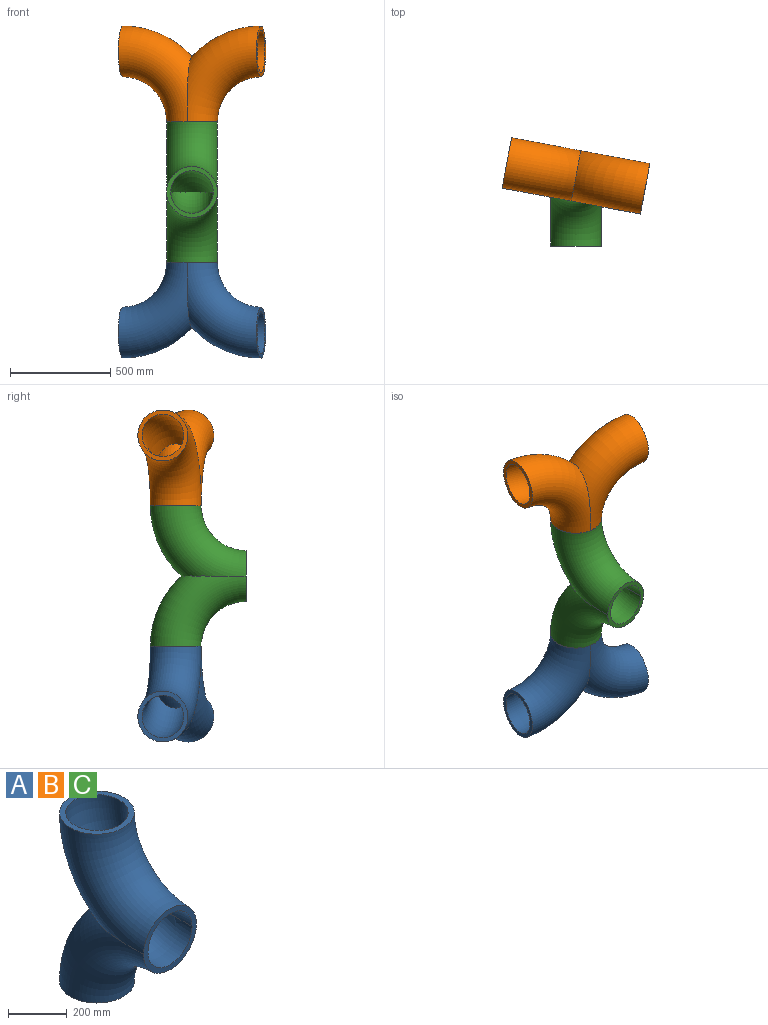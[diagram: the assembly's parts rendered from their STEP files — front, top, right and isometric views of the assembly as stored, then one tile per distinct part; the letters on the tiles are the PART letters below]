
ASSEMBLY  parts=3 mates=5
PART A: 11 faces, bbox 254x517.5x702.2 mm
  f0: torus R=351.08mm, axis (1,0,0), area 77600.1mm2, adj f3,f10
  f1: torus R=351.08mm, axis (1,0,0), area 240336.9mm2, adj f4,f9
  f2: torus R=351.08mm, axis (1,0,0), area 336108.5mm2, adj f3,f4,f7
  f3: plane 254x254mm, normal (0,-1,0), area 15428.1mm2, adj f0,f2,f7,f10
  f4: plane 254x254mm, normal (0,0,-1), area 15428.1mm2, adj f1,f2
  f5: torus R=351.08mm, axis (1,0,0), area 240340.8mm2, adj f6,f8
  f6: plane 254x254mm, normal (0,0,1), area 15428.1mm2, adj f5,f7
  f7: torus R=351.08mm, axis (1,0,0), area 336121.8mm2, adj f2,f3,f6
  f8: torus R=351.08mm, axis (1,0,0), area 48416.9mm2, adj f5
  f9: torus R=351.08mm, axis (1,0,0), area 48414.9mm2, adj f1
  f10: torus R=351.08mm, axis (1,0,0), area 77609.6mm2, adj f0,f3
PART B: same geometry as A
PART C: same geometry as A
PLACE A rot(axis=(-0.51,0.61,-0.61),126.3deg) t=(-404.48,689.43,29.83)mm
PLACE B rot(axis=(0.51,-0.61,-0.61),126.3deg) t=(-404.48,689.43,732)mm
PLACE C t=(-404.48,338.34,380.91)mm fixed
MATE cylindrical C.f6 <-> B.f3  axis (0,0,1) through (-404.48,689.43,732)mm
MATE planar B.f3 <-> C.f6  axis (0,0,-1) through (-404.48,689.43,732)mm
MATE cylindrical A.f3 <-> C.f4  axis (0,0,1) through (-404.48,689.43,29.83)mm
MATE planar C.f4 <-> A.f3  axis (0,0,-1) through (-404.48,689.43,29.83)mm
MATE planar A.f6 <-> B.f4  axis (0.98,-0.18,0) through (-59.39,624.8,-321.26)mm
